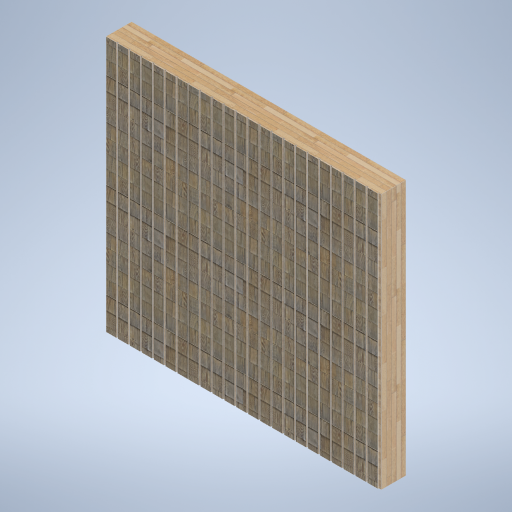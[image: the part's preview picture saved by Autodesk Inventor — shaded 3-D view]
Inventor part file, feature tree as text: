
AUTODESK INVENTOR PART (.ipt)
format: ipt  version: 2024.2 (Build 282272000, 272)  size: 595,968 bytes
history: native  units: mm
features: extrude x2, sketch x2
ambient origin geometry x8: Origin, YZ Plane, XZ Plane, XY Plane, X Axis, Y Axis, Z Axis, Center Point
bodies: Solid1 (feature_tree)
feature tree (4):
  extrude  "Extrusion1"  Depth=120.0mm
  extrude  "Extrusion2"  Depth=120.0mm
  sketch  "Sketch2"  dims[d0=300.0mm d1=0.0mm d2=120.0mm]
  sketch  "Sketch3"  dims[d3=90.0deg d4=120.0mm d5=120.0mm d6=120.0mm d7=120.0mm d8=120.0mm d9=120.0mm d10=120.0mm d11=120.0mm d12=120.0mm d13=120.0mm d14=120.0mm d15=120.0mm d16=120.0mm d17=120.0mm d18=120.0mm d19=120.0mm d20=120.0mm d21=120.0mm d22=120.0mm d23=120.0mm d24=120.0mm d25=120.0mm d26=0.0mm d27=0.0mm]
